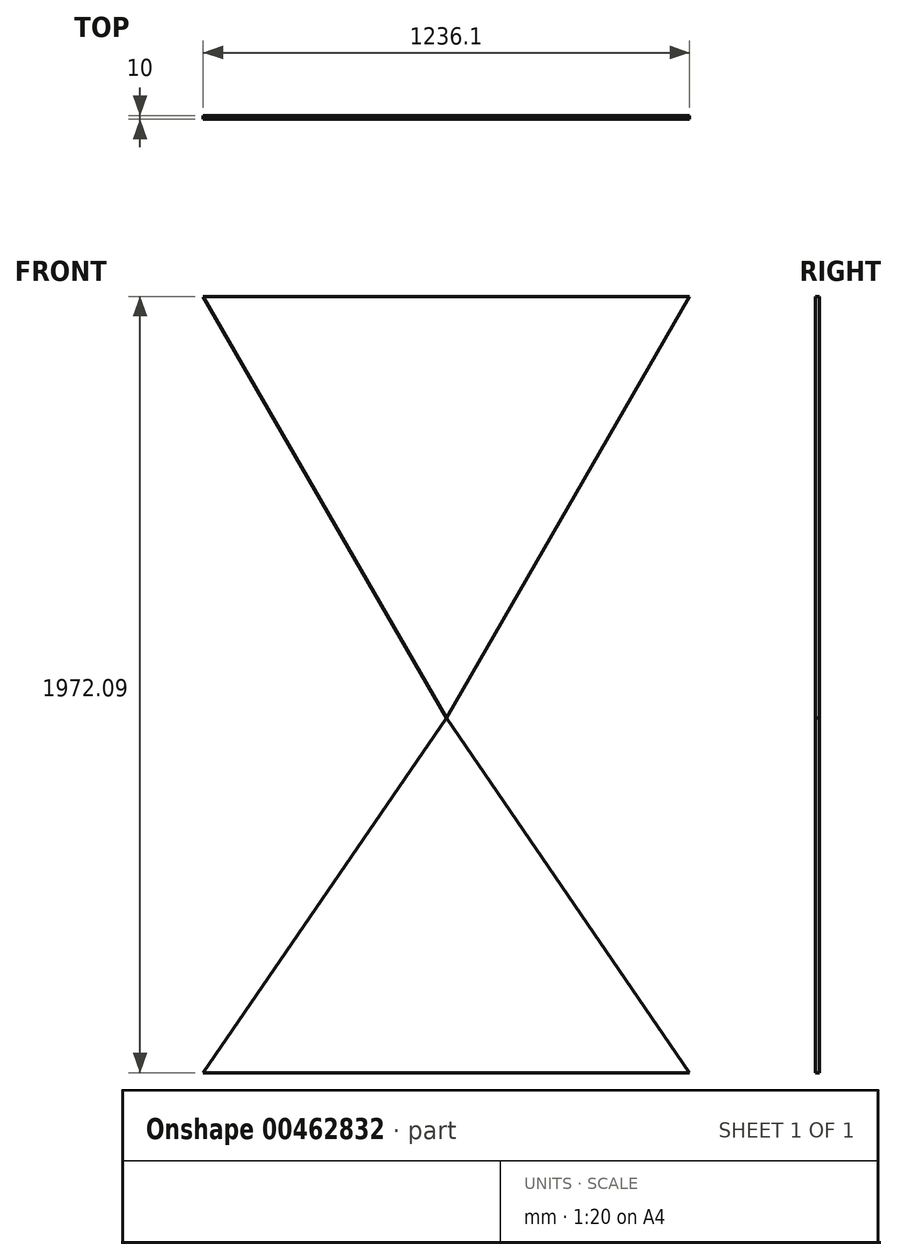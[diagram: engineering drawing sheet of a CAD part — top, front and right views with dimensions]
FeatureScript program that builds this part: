
annotation { "Feature Type Name" : "Feature", "Feature Type Description" : "" }
export const myFeature = defineFeature(function(context is Context, id is Id, definition is map)
    precondition{}
    {
        {
            assignVariable(context, id + "F0", {"name" : "Thickness", "anyValue" : 10});
        }
        {
            var Q0;
            Q0=qCreatedBy(makeId("Front.planeOp"),FACE);
            var sketch = newSketch(context, id + "F1", { "sketchPlane" : qUnion([Q0])});
            skCircle(sketch, "E0.cCircle", {"center": v(0, 0) * mm, "radius": 713.66 * mm, "construction": true});
            skLineSegment(sketch, "E0.0", {"start": v(618.05, 356.83) * mm, "end": v(0, -713.66) * mm});
            skLineSegment(sketch, "E0.1", {"start": v(0, -713.66) * mm, "end": v(-618.05, 356.83) * mm});
            skLineSegment(sketch, "E0.2", {"start": v(-618.05, 356.83) * mm, "end": v(618.05, 356.83) * mm});
            skLineSegment(sketch, "E1", {"start": v(0, 356.83) * mm, "end": v(0, -713.66) * mm, "construction": true});
            skPoint(sketch, "E1.startSnap0", {"position": v(0, 356.83) * mm});
            skSolve(sketch);
        }
        {
            var Q0;
            Q0=makeQuery(id+"F1.imprint","IMPRINT",FACE,{"disambiguationData":[TD([[makeQuery(id+"F1.imprint","IMPRINT",EDGE,{"derivedFrom":sQuery(id+"F1.wireOp",EDGE,"E0.0")}),-1.0]])]});
            extrude(context, id + "F2", {"entities" : qUnion([Q0]), "depth" : (getVariable(context, 'Thickness')) * mm});
        }
        {
            var Q0;
            Q0=qCreatedBy(makeId("Front.planeOp"),FACE);
            var sketch = newSketch(context, id + "F3", { "sketchPlane" : qUnion([Q0])});
            skLineSegment(sketch, "E2", {"start": v(-618.05, -1615.26) * mm, "end": v(618.05, -1615.26) * mm});
            skLineSegment(sketch, "E3", {"start": v(618.05, -1615.26) * mm, "end": v(0, -713.66) * mm});
            skPoint(sketch, "E3.endSnap0", {"position": v(0, -1615.26) * mm});
            skLineSegment(sketch, "E4", {"start": v(0, -713.66) * mm, "end": v(-618.05, -1615.26) * mm});
            skPoint(sketch, "E5.0", {"position": v(0, -713.66) * mm});
            skSolve(sketch);
        }
        {
            var Q0;
            Q0 = qSketchRegion(id + "F3", true);
            extrude(context, id + "F4", {"entities" : qUnion([Q0]), "depth" : (getVariable(context, 'Thickness')) * mm});
        }
    });
